# Revit family: Door_SS_The Sliding Door Company_Wall Slide to Column_Single Panel Single Track (Surface Mount)
name_source: partatom
category: Doors
units: mm (PartAtom-declared; Revit-internal decimal feet)

## family parameters
Always vertical = Yes
Cut with Voids When Loaded = No
Host = Wall
OmniClass Number = 23.30.10.00
OmniClass Title = Doors
Room Calculation Point = No
Shared = No

## types (1)
- Suspended Wall Slide to Column Single Panel & Track (Surface Mounted)
    ADA Opening Clearance = Minimum of 32 inches Opening Clearance
    Analytic Construction = <None>
    Description = Suspended Wall Slide to Column Single Panel & Track (Surface Mounted)
    Finished Opening Height = 101"
    Function = Interior
    Height = 104 1/2"
    Manufacturer = The Sliding Door Company
    Maximum Order Height = 108 inches
    Maximum Order Width = 51 inches
    Model = Suspended Wall Slide to Column Single Panel & Track (Surface Mounted)
    Mounting Bracket Material = TSDC - Anodized Aluminum Silver
    Opening Clearance Height = 100 7/8"
    Opening Clearance Width = 35"
    Order Height = 104 1/2"
    Order Width = 40"
    Panel Height = 101 1/8"
    Panel Width = 40"
    Stile/Rail = 2 1/2"
    Suspended System Frame = Available only in 2.5 inches
    Thickness = 1 1/4"
    Track Length = 77 1/2"
    URL = https://www.slidingdoorco.com
    Wall Closure = By host
    Width = 40"
    With Column = Yes
    Without Column = No

## geometry (parser evidence)
native form markers: Sweep x13
no freeform markers — native parametric forms only
